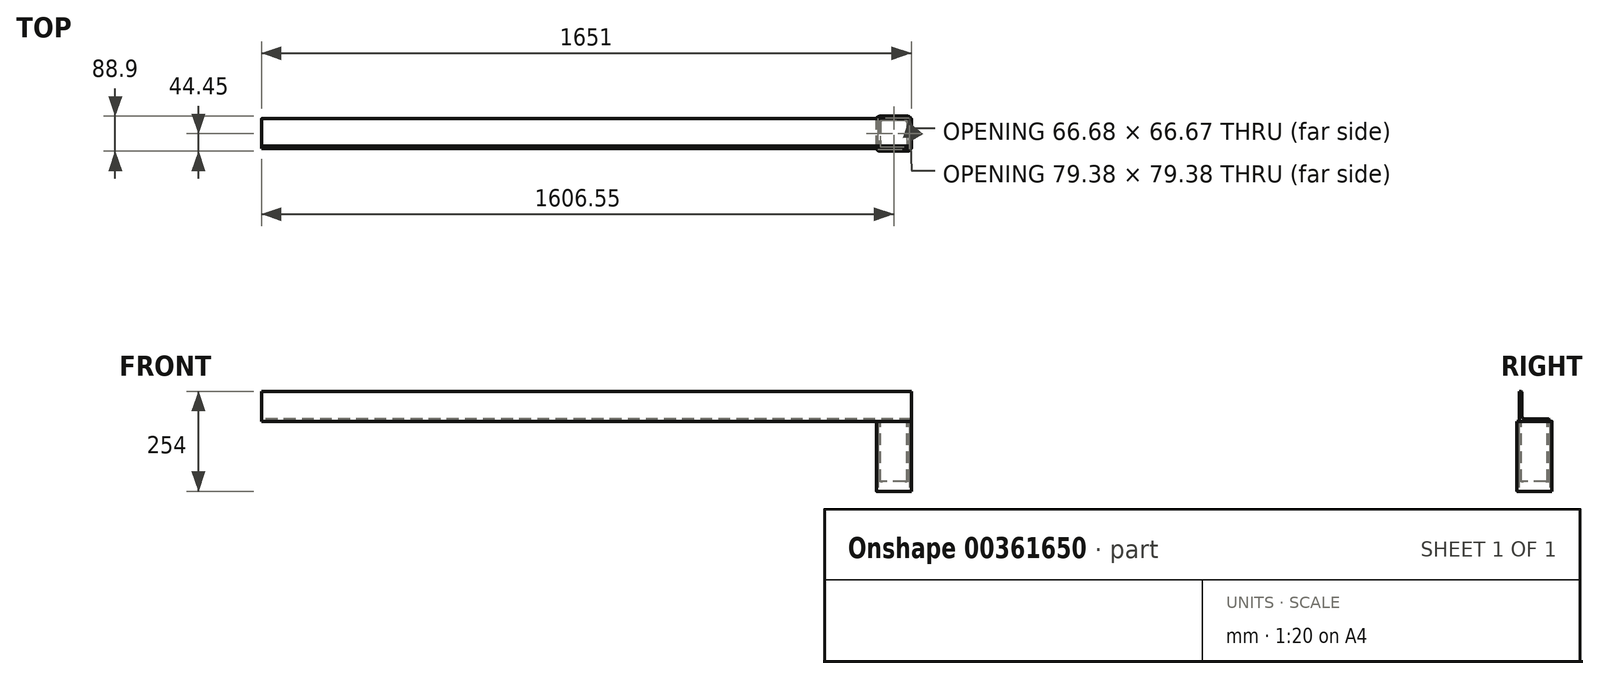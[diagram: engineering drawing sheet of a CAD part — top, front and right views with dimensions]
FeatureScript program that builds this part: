
annotation { "Feature Type Name" : "Feature", "Feature Type Description" : "" }
export const myFeature = defineFeature(function(context is Context, id is Id, definition is map)
    precondition{}
    {
        {
            var Q0;
            Q0=qCreatedBy(makeId("Right.planeOp"),FACE);
            var sketch = newSketch(context, id + "F0", { "sketchPlane" : qUnion([Q0])});
            skLineSegment(sketch, "E0", {"start": v(0, 0) * mm, "end": v(0, 76.2) * mm});
            skLineSegment(sketch, "E1", {"start": v(0, 0) * mm, "end": v(76.2, 0) * mm});
            skLineSegment(sketch, "E2.0", {"start": v(6.35, 6.35) * mm, "end": v(6.35, 76.2) * mm});
            skLineSegment(sketch, "E2.1", {"start": v(6.35, 6.35) * mm, "end": v(76.2, 6.35) * mm});
            skLineSegment(sketch, "E3", {"start": v(0, 76.2) * mm, "end": v(6.35, 76.2) * mm});
            skLineSegment(sketch, "E4", {"start": v(76.2, 0) * mm, "end": v(76.2, 6.35) * mm});
            skSolve(sketch);
        }
        {
            var Q0;
            Q0=makeQuery(id+"F0.imprint","IMPRINT",FACE,{"disambiguationData":[TD([[makeQuery(id+"F0.imprint","IMPRINT",EDGE,{"derivedFrom":sQuery(id+"F0.wireOp",EDGE,"E0")}),-1.0]])]});
            extrude(context, id + "F1", {"entities" : qUnion([Q0]), "endBound" : BoundingType.SYMMETRIC, "depth" : 1651 * mm});
        }
        {
            var Q0;
            Q0=makeQuery(id+"F1.opExtrude","SWEPT_EDGE",EDGE,{"disambiguationData":[OSD([sQuery(id+"F0.wireOp",EDGE,"E2.0"),sQuery(id+"F0.wireOp",EDGE,"E2.1")])]});
            fillet(context, id + "F2", {"entities" : qUnion([Q0]), "radius" : 6.35 * mm, "tangentPropagation" : true, "allowEdgeOverflow" : false});
        }
        {
            var Q0;
            Q0=makeQuery(id+"F1.opExtrude","SWEPT_EDGE",EDGE,{"disambiguationData":[OSD([sQuery(id+"F0.wireOp",EDGE,"E2.0"),sQuery(id+"F0.wireOp",EDGE,"E3")])]});
            var Q1;
            Q1=makeQuery(id+"F1.opExtrude","SWEPT_EDGE",EDGE,{"disambiguationData":[OSD([sQuery(id+"F0.wireOp",EDGE,"E2.1"),sQuery(id+"F0.wireOp",EDGE,"E4")])]});
            fillet(context, id + "F3", {"entities" : qUnion([Q0, Q1]), "radius" : 3.17 * mm, "tangentPropagation" : true, "allowEdgeOverflow" : false});
        }
        {
            var Q0;
            Q0=makeQuery(id+"F1.opExtrude","SWEPT_FACE",FACE,{"disambiguationData":[OSD([sQuery(id+"F0.wireOp",EDGE,"E1")])]});
            var sketch = newSketch(context, id + "F4", { "sketchPlane" : qUnion([Q0])});
            skLineSegment(sketch, "E5.0.0", {"start": v(-825.5, 0) * mm, "end": v(-825.5, -76.2) * mm, "construction": true});
            skLineSegment(sketch, "E5.0.1", {"start": v(-825.5, -76.2) * mm, "end": v(825.5, -76.2) * mm, "construction": true});
            skLineSegment(sketch, "E5.0.2", {"start": v(825.5, -76.2) * mm, "end": v(825.5, 0) * mm, "construction": true});
            skLineSegment(sketch, "E5.0.3", {"start": v(825.5, 0) * mm, "end": v(-825.5, 0) * mm, "construction": true});
            skLineSegment(sketch, "E6.0", {"start": v(819.15, -76.2) * mm, "end": v(819.15, 0) * mm});
            skLineSegment(sketch, "E7", {"start": v(819.15, -76.2) * mm, "end": v(742.95, -76.2) * mm});
            skLineSegment(sketch, "E8", {"start": v(742.95, -76.2) * mm, "end": v(742.95, 0) * mm});
            skLineSegment(sketch, "E9", {"start": v(742.95, 0) * mm, "end": v(819.15, 0) * mm});
            skSolve(sketch);
        }
        {
            var Q0;
            Q0=makeQuery(id+"F4.imprint","IMPRINT",FACE,{"disambiguationData":[TD([[makeQuery(id+"F4.imprint","IMPRINT",EDGE,{"derivedFrom":sQuery(id+"F4.wireOp",EDGE,"E6.0")}),1.0]])]});
            extrude(context, id + "F5", {"entities" : qUnion([Q0]), "depth" : 152.4 * mm});
        }
        {
            var Q0;
            Q0=makeQuery(id+"F5.opExtrude","SWEPT_EDGE",EDGE,{"disambiguationData":[OSD([sQuery(id+"F0.wireOp",EDGE,"E1"),sQuery(id+"F0.wireOp",EDGE,"E4"),sQuery(id+"F4.wireOp",EDGE,"E7"),sQuery(id+"F4.wireOp",EDGE,"E8")])]});
            var Q1;
            Q1=makeQuery(id+"F5.opExtrude","SWEPT_EDGE",EDGE,{"disambiguationData":[OSD([sQuery(id+"F0.wireOp",EDGE,"E0"),sQuery(id+"F0.wireOp",EDGE,"E1"),sQuery(id+"F4.wireOp",EDGE,"E8"),sQuery(id+"F4.wireOp",EDGE,"E9")])]});
            var Q2;
            Q2=makeQuery(id+"F5.opExtrude","SWEPT_EDGE",EDGE,{"disambiguationData":[OSD([sQuery(id+"F0.wireOp",EDGE,"E1"),sQuery(id+"F0.wireOp",EDGE,"E4"),sQuery(id+"F4.wireOp",EDGE,"E6.0"),sQuery(id+"F4.wireOp",EDGE,"E7")])]});
            var Q3;
            Q3=makeQuery(id+"F5.opExtrude","SWEPT_EDGE",EDGE,{"disambiguationData":[OSD([sQuery(id+"F0.wireOp",EDGE,"E0"),sQuery(id+"F0.wireOp",EDGE,"E1"),sQuery(id+"F4.wireOp",EDGE,"E6.0"),sQuery(id+"F4.wireOp",EDGE,"E9")])]});
            fillet(context, id + "F6", {"entities" : qUnion([Q0, Q1, Q2, Q3]), "radius" : 9.52 * mm, "tangentPropagation" : true, "allowEdgeOverflow" : false});
        }
        {
            var Q0;
            Q0=makeQuery(id+"F5.opExtrude","CAP_FACE",FACE,{"disambiguationData":[OSD([sQuery(id+"F4.wireOp",EDGE,"E6.0"),sQuery(id+"F4.wireOp",EDGE,"E7"),sQuery(id+"F4.wireOp",EDGE,"E8"),sQuery(id+"F4.wireOp",EDGE,"E9")])],"isStart":false});
            var Q1;
            Q1=makeQuery(id+"F5.opExtrude","CAP_FACE",FACE,{"disambiguationData":[OSD([sQuery(id+"F4.wireOp",EDGE,"E6.0"),sQuery(id+"F4.wireOp",EDGE,"E7"),sQuery(id+"F4.wireOp",EDGE,"E8"),sQuery(id+"F4.wireOp",EDGE,"E9")])],"isStart":true});
            shell(context, id + "F7", {"entities" : qUnion([Q0, Q1]), "thickness" : 4.76 * mm});
        }
        {
            var Q0;
            Q0=makeQuery(id+"F1.opExtrude","SWEPT_FACE",FACE,{"disambiguationData":[OSD([sQuery(id+"F0.wireOp",EDGE,"E1")])]});
            var sketch = newSketch(context, id + "F8", { "sketchPlane" : qUnion([Q0])});
            skLineSegment(sketch, "E10.0.0", {"start": v(742.95, 0) * mm, "end": v(742.95, -76.2) * mm, "construction": true});
            skLineSegment(sketch, "E10.0.1", {"start": v(742.95, -76.2) * mm, "end": v(819.15, -76.2) * mm, "construction": true});
            skLineSegment(sketch, "E10.0.2", {"start": v(819.15, -76.2) * mm, "end": v(819.15, 0) * mm, "construction": true});
            skLineSegment(sketch, "E10.0.3", {"start": v(819.15, 0) * mm, "end": v(742.95, 0) * mm, "construction": true});
            skLineSegment(sketch, "E11.bottom", {"start": v(736.6, 6.35) * mm, "end": v(825.5, 6.35) * mm});
            skLineSegment(sketch, "E11.top", {"start": v(736.6, -82.55) * mm, "end": v(825.5, -82.55) * mm});
            skLineSegment(sketch, "E11.left", {"start": v(736.6, 6.35) * mm, "end": v(736.6, -82.55) * mm});
            skLineSegment(sketch, "E11.right", {"start": v(825.5, 6.35) * mm, "end": v(825.5, -82.55) * mm});
            skPoint(sketch, "E11.middle", {"position": v(781.05, -38.1) * mm});
            skPoint(sketch, "E12", {"position": v(819.15, -38.1) * mm});
            skPoint(sketch, "E13", {"position": v(781.05, -76.2) * mm});
            skSolve(sketch);
        }
        {
            var Q0;
            {var subQ0=sQuery(id+"F8.wireOp",EDGE,"E11.bottom");Q0=makeQuery(id+"F8.imprint","IMPRINT",FACE,{"disambiguationData":[TD([[makeQuery(id+"F8.imprint","IMPRINT",EDGE,{"derivedFrom":subQ0}),-1.0]])]});}
            var Q1;
            {var subQ0=sQuery(id+"F8.wireOp",EDGE,"E11.left");var subQ1=sQuery(id+"F0.wireOp",EDGE,"E1");var subQ2=makeQuery(id+"F1.opExtrude","SWEPT_EDGE",EDGE,{"disambiguationData":[OSD([sQuery(id+"F0.wireOp",EDGE,"E0"),subQ1])]});var subQ3=makeQuery(id+"F8.imprint","INTERSECT",VERTEX,{"derivedFrom":[subQ2,subQ0]});Q1=makeQuery(id+"F8.imprint","IMPRINT",FACE,{"disambiguationData":[TD([[makeQuery(id+"F8.imprint","IMPRINT",EDGE,{"disambiguationData":[TD([[subQ3,-1.0]])],"derivedFrom":subQ0}),1.0]])]});}
            var Q2;
            {var subQ0=sQuery(id+"F8.wireOp",EDGE,"E11.top");Q2=makeQuery(id+"F8.imprint","IMPRINT",FACE,{"disambiguationData":[TD([[makeQuery(id+"F8.imprint","IMPRINT",EDGE,{"derivedFrom":subQ0}),1.0]])]});}
            extrude(context, id + "F9", {"entities" : qUnion([Q0, Q1, Q2]), "depth" : 177.8 * mm});
        }
        {
            var Q0;
            Q0=makeQuery(id+"F9.opExtrude","SWEPT_EDGE",EDGE,{"disambiguationData":[OSD([sQuery(id+"F8.wireOp",EDGE,"E11.top"),sQuery(id+"F8.wireOp",EDGE,"E11.right")])]});
            var Q1;
            Q1=makeQuery(id+"F9.opExtrude","SWEPT_EDGE",EDGE,{"disambiguationData":[OSD([sQuery(id+"F8.wireOp",EDGE,"E11.top"),sQuery(id+"F8.wireOp",EDGE,"E11.left")])]});
            var Q2;
            Q2=makeQuery(id+"F9.opExtrude","SWEPT_EDGE",EDGE,{"disambiguationData":[OSD([sQuery(id+"F8.wireOp",EDGE,"E11.bottom"),sQuery(id+"F8.wireOp",EDGE,"E11.left")])]});
            var Q3;
            Q3=makeQuery(id+"F9.opExtrude","SWEPT_EDGE",EDGE,{"disambiguationData":[OSD([sQuery(id+"F8.wireOp",EDGE,"E11.bottom"),sQuery(id+"F8.wireOp",EDGE,"E11.right")])]});
            fillet(context, id + "F10", {"entities" : qUnion([Q0, Q1, Q2, Q3]), "radius" : 9.52 * mm, "tangentPropagation" : true, "allowEdgeOverflow" : false});
        }
        {
            var Q0;
            Q0=makeQuery(id+"F9.opExtrude","CAP_FACE",FACE,{"disambiguationData":[OSD([sQuery(id+"F8.wireOp",EDGE,"E11.bottom"),sQuery(id+"F8.wireOp",EDGE,"E11.top"),sQuery(id+"F8.wireOp",EDGE,"E11.left"),sQuery(id+"F8.wireOp",EDGE,"E11.right")])],"isStart":false});
            var Q1;
            Q1=makeQuery(id+"F9.opExtrude","CAP_FACE",FACE,{"disambiguationData":[OSD([sQuery(id+"F8.wireOp",EDGE,"E11.bottom"),sQuery(id+"F8.wireOp",EDGE,"E11.top"),sQuery(id+"F8.wireOp",EDGE,"E11.left"),sQuery(id+"F8.wireOp",EDGE,"E11.right")])],"isStart":true});
            shell(context, id + "F11", {"entities" : qUnion([Q0, Q1]), "thickness" : 4.76 * mm});
        }
    });
